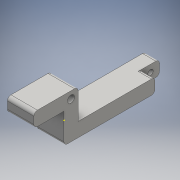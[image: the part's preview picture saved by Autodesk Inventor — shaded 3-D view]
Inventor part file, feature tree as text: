
AUTODESK INVENTOR PART (.ipt)
format: ipt  version: 2016 (Build 200138000, 138)  size: 157,696 bytes
history: native  units: mm
features: sketch x7, extrude x4, fillet x3, hole x2
ambient origin geometry x8: Origin, YZ Plane, XZ Plane, XY Plane, X Axis, Y Axis, Z Axis, Center Point
bodies: Solid1 (feature_tree)
feature tree (16):
  extrude  "Extrusion1"  Depth=25.0mm
  hole  "Hole1"  [1 undecoded]
  sketch  "Sketch4"  dims[d6=4.0mm]
  extrude  "Extrusion3"  Depth=8.0mm
  fillet  "Fillet3"  Radius=17.0mm
  extrude  "Extrusion4"  Depth=2.0mm
  fillet  "Fillet4"  Radius=8.0mm
  extrude  "Extrusion5"  Depth=15.0mm TaperAngle=0.0deg
  hole  "Hole2"  [1 undecoded]
  fillet  "Fillet5"  Radius=7.5mm
  sketch  "Sketch1"  dims[d0=15.0mm d1=25.0mm]
  sketch  "Sketch2"  dims[d2=8.0mm d3=0.0mm d5=4.0mm]
  sketch  "Sketch5"  dims[d7=4.0mm d8=6.0mm d9=4.0mm d10=2.0mm d11=90.0deg d12=8.0mm d13=20.594885mm d20=8.0mm d21=17.0mm]
  sketch  "Sketch6"  dims[d22=15.0mm d23=0.0mm d24=2.0mm d25=8.0mm]
  sketch  "Sketch7"  dims[d26=53.5mm d27=15.0mm d28=0.0mm]
  sketch  "Sketch8"  dims[d29=2.0mm d30=10.0mm d31=7.5mm d32=0.0mm d33=4.0mm d34=5.0mm d35=3.0mm d36=6.0mm d37=4.0mm d38=2.0mm d39=90.0deg d40=8.0mm d41=20.594885mm d42=2.0mm d43=0.0mm]
note: 2 required parameter values undecoded (feature->parameter linkage not recoverable at this tier; creation-order binding heuristic only, values carry confidence <= 0.55)
